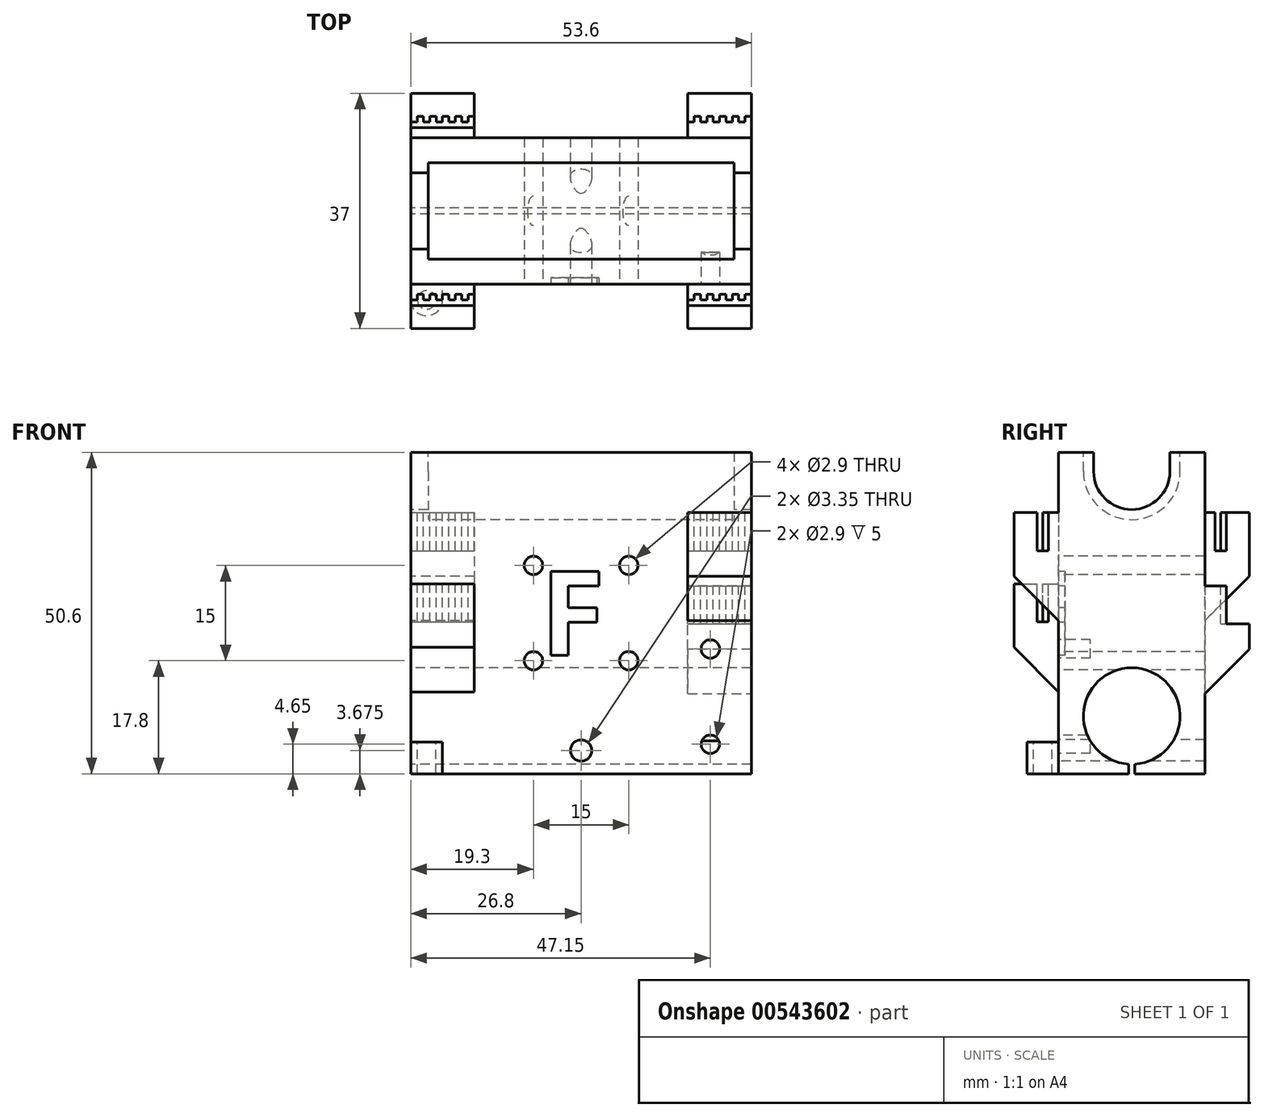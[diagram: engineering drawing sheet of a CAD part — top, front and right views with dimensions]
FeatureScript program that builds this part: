
annotation { "Feature Type Name" : "Feature", "Feature Type Description" : "" }
export const myFeature = defineFeature(function(context is Context, id is Id, definition is map)
    precondition{}
    {
        {
            assignVariable(context, id + "F0", {"name" : "LM8LUU", "anyValue" : 1.8});
        }
        {
            var Q0;
            Q0=qCreatedBy(makeId("Top.planeOp"),FACE);
            var sketch = newSketch(context, id + "F1", { "sketchPlane" : qUnion([Q0])});
            skLineSegment(sketch, "E0.bottom", {"start": v(0, 0) * mm, "end": v(53.6, 0) * mm});
            skLineSegment(sketch, "E0.top", {"start": v(0, 23) * mm, "end": v(53.6, 23) * mm});
            skLineSegment(sketch, "E0.left", {"start": v(0, 0) * mm, "end": v(0, 23) * mm});
            skLineSegment(sketch, "E0.right", {"start": v(53.6, 0) * mm, "end": v(53.6, 23) * mm});
            skSolve(sketch);
        }
        {
            var Q0;
            Q0=qSketchRegion(id+"F1",true);
            extrude(context, id + "F2", {"entities" : qUnion([Q0]), "depth" : 50.6 * mm});
        }
        {
            var Q0;
            Q0=makeQuery(id+"F2.opExtrude","SWEPT_FACE",FACE,{"disambiguationData":[OSD([sQuery(id+"F1.wireOp",EDGE,"E0.left")])]});
            var sketch = newSketch(context, id + "F3", { "sketchPlane" : qUnion([Q0])});
            skCircle(sketch, "E1", {"center": v(-11.5, 9.1) * mm, "radius": 7.6 * mm});
            skCircle(sketch, "E2", {"center": v(-11.5, 47.6) * mm, "radius": 6 * mm});
            skLineSegment(sketch, "E3", {"start": v(-23, 47.6) * mm, "end": v(0, 47.6) * mm, "construction": true});
            skLineSegment(sketch, "E4", {"start": v(-17.5, 50.6) * mm, "end": v(-17.5, 47.6) * mm});
            skLineSegment(sketch, "E5", {"start": v(-5.5, 50.6) * mm, "end": v(-5.5, 47.6) * mm});
            skLineSegment(sketch, "E6", {"start": v(-23, 9.1) * mm, "end": v(0, 9.1) * mm, "construction": true});
            skLineSegment(sketch, "E7", {"start": v(-11.5, 9.1) * mm, "end": v(-11.5, 0) * mm, "construction": true});
            skLineSegment(sketch, "E8", {"start": v(-11.5, 0) * mm, "end": v(-12, 0) * mm});
            skLineSegment(sketch, "E9", {"start": v(-12, 0) * mm, "end": v(-12, 1.52) * mm});
            skLineSegment(sketch, "E10", {"start": v(-12, 1.52) * mm, "end": v(-11, 1.52) * mm});
            skLineSegment(sketch, "E11", {"start": v(-11, 1.52) * mm, "end": v(-11, 0) * mm});
            skLineSegment(sketch, "E12", {"start": v(-11, 0) * mm, "end": v(-11.5, 0) * mm});
            skLineSegment(sketch, "E13", {"start": v(-11.5, 15.6) * mm, "end": v(-11.5, 16.7) * mm});
            skLineSegment(sketch, "E14", {"start": v(-11.5, 15.6) * mm, "end": v(-7, 15.22) * mm});
            skLineSegment(sketch, "E15", {"start": v(-11.5, 15.6) * mm, "end": v(-16, 15.22) * mm});
            skCircle(sketch, "E16", {"center": v(-11.5, 47.6) * mm, "radius": 7.6 * mm});
            skLineSegment(sketch, "E17", {"start": v(-3.9, 47.6) * mm, "end": v(-3.9, 50.6) * mm});
            skLineSegment(sketch, "E18", {"start": v(-19.1, 47.6) * mm, "end": v(-19.1, 50.6) * mm});
            skSolve(sketch);
        }
        {
            var Q0;
            {var subQ0=sQuery(id+"F3.wireOp",EDGE,"E14");var subQ1=sQuery(id+"F3.wireOp",EDGE,"E1");var subQ3=makeQuery(id+"F3.imprint","INTERSECT",VERTEX,{"disambiguationData":[OD(0.0)],"derivedFrom":[subQ1,subQ0]});Q0=makeQuery(id+"F3.imprint","IMPRINT",FACE,{"disambiguationData":[TD([[makeQuery(id+"F3.imprint","IMPRINT",EDGE,{"disambiguationData":[TD([[subQ3,-1.0]])],"derivedFrom":subQ1}),1.0]])]});}
            var Q1;
            {var subQ0=sQuery(id+"F3.wireOp",EDGE,"E15");var subQ1=sQuery(id+"F3.wireOp",EDGE,"E1");var subQ3=makeQuery(id+"F3.imprint","INTERSECT",VERTEX,{"disambiguationData":[OD(0.0)],"derivedFrom":[subQ1,subQ0]});Q1=makeQuery(id+"F3.imprint","IMPRINT",FACE,{"disambiguationData":[TD([[makeQuery(id+"F3.imprint","IMPRINT",EDGE,{"disambiguationData":[TD([[subQ3,1.0]])],"derivedFrom":subQ1}),1.0]])]});}
            var Q2;
            Q2=makeQuery(id+"F3.imprint","IMPRINT",FACE,{"disambiguationData":[TD([[makeQuery(id+"F3.imprint","IMPRINT",EDGE,{"derivedFrom":sQuery(id+"F3.wireOp",EDGE,"E8")}),-1.0]])]});
            var Q3;
            {var subQ0=sQuery(id+"F3.wireOp",EDGE,"E10");Q3=makeQuery(id+"F3.imprint","IMPRINT",FACE,{"disambiguationData":[TD([[makeQuery(id+"F3.imprint","IMPRINT",EDGE,{"derivedFrom":subQ0}),-1.0]])]});}
            var Q4;
            {var subQ3=sQuery(id+"F3.wireOp",EDGE,"E13");Q4=makeQuery(id+"F3.imprint","IMPRINT",FACE,{"disambiguationData":[TD([[makeQuery(id+"F3.imprint","IMPRINT",EDGE,{"derivedFrom":subQ3}),-1.0]])]});}
            var Q5;
            {var subQ3=sQuery(id+"F3.wireOp",EDGE,"E13");Q5=makeQuery(id+"F3.imprint","IMPRINT",FACE,{"disambiguationData":[TD([[makeQuery(id+"F3.imprint","IMPRINT",EDGE,{"derivedFrom":subQ3}),1.0]])]});}
            var Q6;
            {var subQ7=sQuery(id+"F3.wireOp",EDGE,"E10");Q6=makeQuery(id+"F3.imprint","IMPRINT",FACE,{"disambiguationData":[TD([[makeQuery(id+"F3.imprint","IMPRINT",EDGE,{"derivedFrom":subQ7}),1.0]])]});}
            var Q7;
            {var subQ3=sQuery(id+"F3.wireOp",EDGE,"E5");Q7=makeQuery(id+"F3.imprint","IMPRINT",FACE,{"disambiguationData":[TD([[makeQuery(id+"F3.imprint","IMPRINT",EDGE,{"derivedFrom":subQ3}),-1.0]])]});}
            var Q8;
            {var subQ0=sQuery(id+"F3.wireOp",EDGE,"E4");Q8=makeQuery(id+"F3.imprint","IMPRINT",FACE,{"disambiguationData":[TD([[makeQuery(id+"F3.imprint","IMPRINT",EDGE,{"derivedFrom":subQ0}),1.0]])]});}
            var Q9;
            {var subQ0=sQuery(id+"F3.wireOp",EDGE,"E4");Q9=makeQuery(id+"F3.imprint","IMPRINT",FACE,{"disambiguationData":[TD([[makeQuery(id+"F3.imprint","IMPRINT",EDGE,{"derivedFrom":subQ0}),1.0]])]});}
            var Q10;
            {var subQ3=sQuery(id+"F3.wireOp",EDGE,"E5");Q10=makeQuery(id+"F3.imprint","IMPRINT",FACE,{"disambiguationData":[TD([[makeQuery(id+"F3.imprint","IMPRINT",EDGE,{"derivedFrom":subQ3}),-1.0]])]});}
            var Q11;
            {var subQ1=sQuery(id+"F3.wireOp",EDGE,"E2");var subQ4=makeQuery(id+"F3.imprint","INTERSECT",VERTEX,{"derivedFrom":[subQ1,sQuery(id+"F3.wireOp",EDGE,"E5")]});Q11=makeQuery(id+"F3.imprint","IMPRINT",FACE,{"disambiguationData":[TD([[makeQuery(id+"F3.imprint","IMPRINT",EDGE,{"disambiguationData":[TD([[subQ4,-1.0]])],"derivedFrom":subQ1}),1.0]])]});}
            extrude(context, id + "F4", {"entities" : qUnion([Q0, Q1, Q2, Q3, Q4, Q5, Q6, Q7, Q8, Q9, Q10, Q11]), "operationType" : NewBodyOperationType.REMOVE, "endBound" : BoundingType.THROUGH_ALL, "oppositeDirection" : true, "depth" : 25 * mm});
        }
        {
            var Q0;
            {var subQ3=sQuery(id+"F3.wireOp",EDGE,"E4");Q0=makeQuery(id+"F3.imprint","IMPRINT",FACE,{"disambiguationData":[TD([[makeQuery(id+"F3.imprint","IMPRINT",EDGE,{"derivedFrom":subQ3}),-1.0]])]});}
            var Q1;
            {var subQ3=sQuery(id+"F3.wireOp",EDGE,"E18");Q1=makeQuery(id+"F3.imprint","IMPRINT",FACE,{"disambiguationData":[TD([[makeQuery(id+"F3.imprint","IMPRINT",EDGE,{"derivedFrom":subQ3}),-1.0]])]});}
            var Q2;
            {var subQ3=sQuery(id+"F3.wireOp",EDGE,"E17");Q2=makeQuery(id+"F3.imprint","IMPRINT",FACE,{"disambiguationData":[TD([[makeQuery(id+"F3.imprint","IMPRINT",EDGE,{"derivedFrom":subQ3}),1.0]])]});}
            extrude(context, id + "F5", {"entities" : qUnion([Q0, Q1, Q2]), "operationType" : NewBodyOperationType.REMOVE, "oppositeDirection" : true, "depth" : (46.25 + getVariable(context, 'LM8LUU') * 2) * mm});
        }
        {
            var Q0;
            {var subQ3=sQuery(id+"F3.wireOp",EDGE,"E4");Q0=makeQuery(id+"F3.imprint","IMPRINT",FACE,{"disambiguationData":[TD([[makeQuery(id+"F3.imprint","IMPRINT",EDGE,{"derivedFrom":subQ3}),-1.0]])]});}
            var Q1;
            {var subQ3=sQuery(id+"F3.wireOp",EDGE,"E18");Q1=makeQuery(id+"F3.imprint","IMPRINT",FACE,{"disambiguationData":[TD([[makeQuery(id+"F3.imprint","IMPRINT",EDGE,{"derivedFrom":subQ3}),-1.0]])]});}
            var Q2;
            {var subQ3=sQuery(id+"F3.wireOp",EDGE,"E17");Q2=makeQuery(id+"F3.imprint","IMPRINT",FACE,{"disambiguationData":[TD([[makeQuery(id+"F3.imprint","IMPRINT",EDGE,{"derivedFrom":subQ3}),1.0]])]});}
            extrude(context, id + "F6", {"entities" : qUnion([Q0, Q1, Q2]), "operationType" : NewBodyOperationType.ADD, "oppositeDirection" : true, "depth" : (26.75 - getVariable(context, 'LM8LUU')) * mm});
        }
        {
            var Q0;
            {var subQ3=sQuery(id+"F3.wireOp",EDGE,"E4");Q0=makeQuery(id+"F3.imprint","IMPRINT",FACE,{"disambiguationData":[TD([[makeQuery(id+"F3.imprint","IMPRINT",EDGE,{"derivedFrom":subQ3}),-1.0]])]});}
            var Q1;
            {var subQ3=sQuery(id+"F3.wireOp",EDGE,"E18");Q1=makeQuery(id+"F3.imprint","IMPRINT",FACE,{"disambiguationData":[TD([[makeQuery(id+"F3.imprint","IMPRINT",EDGE,{"derivedFrom":subQ3}),-1.0]])]});}
            var Q2;
            {var subQ3=sQuery(id+"F3.wireOp",EDGE,"E17");Q2=makeQuery(id+"F3.imprint","IMPRINT",FACE,{"disambiguationData":[TD([[makeQuery(id+"F3.imprint","IMPRINT",EDGE,{"derivedFrom":subQ3}),1.0]])]});}
            extrude(context, id + "F7", {"entities" : qUnion([Q0, Q1, Q2]), "operationType" : NewBodyOperationType.REMOVE, "oppositeDirection" : true, "depth" : (23.25 + getVariable(context, 'LM8LUU')) * mm});
        }
        {
            var Q0;
            {var subQ3=sQuery(id+"F3.wireOp",EDGE,"E4");Q0=makeQuery(id+"F3.imprint","IMPRINT",FACE,{"disambiguationData":[TD([[makeQuery(id+"F3.imprint","IMPRINT",EDGE,{"derivedFrom":subQ3}),-1.0]])]});}
            var Q1;
            {var subQ3=sQuery(id+"F3.wireOp",EDGE,"E18");Q1=makeQuery(id+"F3.imprint","IMPRINT",FACE,{"disambiguationData":[TD([[makeQuery(id+"F3.imprint","IMPRINT",EDGE,{"derivedFrom":subQ3}),-1.0]])]});}
            var Q2;
            {var subQ3=sQuery(id+"F3.wireOp",EDGE,"E17");Q2=makeQuery(id+"F3.imprint","IMPRINT",FACE,{"disambiguationData":[TD([[makeQuery(id+"F3.imprint","IMPRINT",EDGE,{"derivedFrom":subQ3}),1.0]])]});}
            extrude(context, id + "F8", {"entities" : qUnion([Q0, Q1, Q2]), "operationType" : NewBodyOperationType.ADD, "oppositeDirection" : true, "depth" : 3.75 * mm});
        }
        {
            var Q0;
            Q0=makeQuery(id+"F2.opExtrude","SWEPT_FACE",FACE,{"disambiguationData":[OSD([sQuery(id+"F1.wireOp",EDGE,"E0.bottom")])]});
            var sketch = newSketch(context, id + "F9", { "sketchPlane" : qUnion([Q0])});
            skLineSegment(sketch, "E19.bottom", {"start": v(0, 29.9) * mm, "end": v(10, 29.9) * mm});
            skLineSegment(sketch, "E19.top", {"start": v(0, 9.9) * mm, "end": v(10, 9.9) * mm});
            skLineSegment(sketch, "E19.left", {"start": v(0, 29.9) * mm, "end": v(0, 9.9) * mm});
            skLineSegment(sketch, "E19.right", {"start": v(10, 29.9) * mm, "end": v(10, 9.9) * mm});
            skLineSegment(sketch, "E20.bottom", {"start": v(53.6, 41.1) * mm, "end": v(43.6, 41.1) * mm});
            skLineSegment(sketch, "E20.top", {"start": v(53.6, 21.1) * mm, "end": v(43.6, 21.1) * mm});
            skLineSegment(sketch, "E20.left", {"start": v(53.6, 41.1) * mm, "end": v(53.6, 21.1) * mm});
            skLineSegment(sketch, "E20.right", {"start": v(43.6, 41.1) * mm, "end": v(43.6, 21.1) * mm});
            skPoint(sketch, "E21", {"position": v(0, 47.6) * mm});
            skPoint(sketch, "E22", {"position": v(0, 9.4) * mm});
            skSolve(sketch);
        }
        {
            var Q0;
            Q0=qSketchRegion(id+"F9",true);
            extrude(context, id + "F10", {"entities" : qUnion([Q0]), "operationType" : NewBodyOperationType.ADD, "depth" : 7 * mm});
        }
        {
            var Q0;
            Q0=makeQuery(id+"F10.opExtrude","CAP_EDGE",EDGE,{"disambiguationData":[OSD([sQuery(id+"F9.wireOp",EDGE,"E19.top")])],"isStart":false});
            var Q1;
            Q1=makeQuery(id+"F10.opExtrude","CAP_EDGE",EDGE,{"disambiguationData":[OSD([sQuery(id+"F9.wireOp",EDGE,"E20.top")])],"isStart":false});
            chamfer(context, id + "F11", {"entities" : qUnion([Q0, Q1]), "width" : 10 * mm, "tangentPropagation" : true});
        }
        {
            var Q0;
            Q0=makeQuery(id+"F10.opExtrude","SWEPT_FACE",FACE,{"disambiguationData":[OSD([sQuery(id+"F9.wireOp",EDGE,"E19.bottom")])]});
            var sketch = newSketch(context, id + "F12", { "sketchPlane" : qUnion([Q0])});
            skLineSegment(sketch, "E23", {"start": v(-935.9, 0) * mm, "end": v(-935.88, -4.54) * mm});
            skLineSegment(sketch, "E24.left", {"start": v(0, -3.4) * mm, "end": v(0, -1.6) * mm});
            skLineSegment(sketch, "E25", {"start": v(6, -2.5) * mm, "end": v(7, -2.5) * mm});
            skLineSegment(sketch, "E26", {"start": v(4, -2.5) * mm, "end": v(5, -2.5) * mm});
            skLineSegment(sketch, "E27", {"start": v(0, -2.5) * mm, "end": v(1, -2.5) * mm});
            skLineSegment(sketch, "E28", {"start": v(7, -1.6) * mm, "end": v(8, -1.6) * mm});
            skLineSegment(sketch, "E29", {"start": v(2, -2.5) * mm, "end": v(3, -2.5) * mm});
            skLineSegment(sketch, "E30", {"start": v(3, -1.6) * mm, "end": v(4, -1.6) * mm});
            skLineSegment(sketch, "E31", {"start": v(8, -2.5) * mm, "end": v(9, -2.5) * mm});
            skLineSegment(sketch, "E32", {"start": v(8, -1.6) * mm, "end": v(8, -2.5) * mm});
            skLineSegment(sketch, "E33", {"start": v(9, -2.5) * mm, "end": v(9, -1.6) * mm});
            skLineSegment(sketch, "E34", {"start": v(10, -1.6) * mm, "end": v(10, -2.5) * mm});
            skLineSegment(sketch, "E35", {"start": v(6, -1.6) * mm, "end": v(6, -2.5) * mm});
            skLineSegment(sketch, "E36", {"start": v(2, -1.6) * mm, "end": v(2, -2.5) * mm});
            skLineSegment(sketch, "E37", {"start": v(1, -1.6) * mm, "end": v(2, -1.6) * mm});
            skLineSegment(sketch, "E38", {"start": v(1, -2.5) * mm, "end": v(1, -1.6) * mm});
            skLineSegment(sketch, "E39", {"start": v(9, -1.6) * mm, "end": v(10, -1.6) * mm});
            skLineSegment(sketch, "E40", {"start": v(5, -1.6) * mm, "end": v(6, -1.6) * mm});
            skLineSegment(sketch, "E41", {"start": v(5, -2.5) * mm, "end": v(5, -1.6) * mm});
            skLineSegment(sketch, "E42", {"start": v(3, -2.5) * mm, "end": v(3, -1.6) * mm});
            skLineSegment(sketch, "E43", {"start": v(4, -1.6) * mm, "end": v(4, -2.5) * mm});
            skLineSegment(sketch, "E44", {"start": v(7, -2.5) * mm, "end": v(7, -1.6) * mm});
            skLineSegment(sketch, "E45", {"start": v(0, -1.6) * mm, "end": v(0, -2.5) * mm});
            skLineSegment(sketch, "E46", {"start": v(10, -2.5) * mm, "end": v(10, -3.4) * mm});
            skLineSegment(sketch, "E47", {"start": v(0, -3.4) * mm, "end": v(10, -3.4) * mm});
            skLineSegment(sketch, "E48", {"start": v(5.3, -1.6) * mm, "end": v(5.3, 0) * mm});
            skSolve(sketch);
        }
        {
            var Q0;
            Q0=qSketchRegion(id+"F12",true);
            extrude(context, id + "F13", {"entities" : qUnion([Q0]), "operationType" : NewBodyOperationType.REMOVE, "oppositeDirection" : true, "depth" : 6 * mm});
        }
        {
            var Q0;
            Q0=makeQuery(id+"F10.opExtrude","SWEPT_FACE",FACE,{"disambiguationData":[OSD([sQuery(id+"F9.wireOp",EDGE,"E20.bottom")])]});
            var sketch = newSketch(context, id + "F14", { "sketchPlane" : qUnion([Q0])});
            skLineSegment(sketch, "E49.left", {"start": v(43.6, -3.4) * mm, "end": v(43.6, -1.6) * mm});
            skLineSegment(sketch, "E50", {"start": v(49.6, -2.5) * mm, "end": v(50.6, -2.5) * mm});
            skLineSegment(sketch, "E51", {"start": v(47.6, -2.5) * mm, "end": v(48.6, -2.5) * mm});
            skLineSegment(sketch, "E52", {"start": v(43.6, -2.5) * mm, "end": v(44.6, -2.5) * mm});
            skLineSegment(sketch, "E53", {"start": v(50.6, -1.6) * mm, "end": v(51.6, -1.6) * mm});
            skLineSegment(sketch, "E54", {"start": v(45.6, -2.5) * mm, "end": v(46.6, -2.5) * mm});
            skLineSegment(sketch, "E55", {"start": v(46.6, -1.6) * mm, "end": v(47.6, -1.6) * mm});
            skLineSegment(sketch, "E56", {"start": v(51.6, -2.5) * mm, "end": v(52.6, -2.5) * mm});
            skLineSegment(sketch, "E57", {"start": v(51.6, -1.6) * mm, "end": v(51.6, -2.5) * mm});
            skLineSegment(sketch, "E58", {"start": v(52.6, -2.5) * mm, "end": v(52.6, -1.6) * mm});
            skLineSegment(sketch, "E59", {"start": v(53.6, -1.6) * mm, "end": v(53.6, -2.5) * mm});
            skLineSegment(sketch, "E60", {"start": v(49.6, -1.6) * mm, "end": v(49.6, -2.5) * mm});
            skLineSegment(sketch, "E61", {"start": v(45.6, -1.6) * mm, "end": v(45.6, -2.5) * mm});
            skLineSegment(sketch, "E62", {"start": v(44.6, -1.6) * mm, "end": v(45.6, -1.6) * mm});
            skLineSegment(sketch, "E63", {"start": v(44.6, -2.5) * mm, "end": v(44.6, -1.6) * mm});
            skLineSegment(sketch, "E64", {"start": v(52.6, -1.6) * mm, "end": v(53.6, -1.6) * mm});
            skLineSegment(sketch, "E65", {"start": v(48.6, -1.6) * mm, "end": v(49.6, -1.6) * mm});
            skLineSegment(sketch, "E66", {"start": v(48.6, -2.5) * mm, "end": v(48.6, -1.6) * mm});
            skLineSegment(sketch, "E67", {"start": v(46.6, -2.5) * mm, "end": v(46.6, -1.6) * mm});
            skLineSegment(sketch, "E68", {"start": v(47.6, -1.6) * mm, "end": v(47.6, -2.5) * mm});
            skLineSegment(sketch, "E69", {"start": v(50.6, -2.5) * mm, "end": v(50.6, -1.6) * mm});
            skLineSegment(sketch, "E70", {"start": v(43.6, -1.6) * mm, "end": v(43.6, -2.5) * mm});
            skLineSegment(sketch, "E71", {"start": v(53.6, -2.5) * mm, "end": v(53.6, -3.4) * mm});
            skLineSegment(sketch, "E72", {"start": v(43.6, -3.4) * mm, "end": v(53.6, -3.4) * mm});
            skLineSegment(sketch, "E73", {"start": v(48.83, -1.6) * mm, "end": v(48.83, 0) * mm});
            skSolve(sketch);
        }
        {
            var Q0;
            Q0=qSketchRegion(id+"F14",true);
            extrude(context, id + "F15", {"entities" : qUnion([Q0]), "operationType" : NewBodyOperationType.REMOVE, "oppositeDirection" : true, "depth" : 6 * mm});
        }
        {
            var Q0;
            Q0=makeQuery(id+"F2.opExtrude","SWEPT_FACE",FACE,{"disambiguationData":[OSD([sQuery(id+"F1.wireOp",EDGE,"E0.top")])]});
            var sketch = newSketch(context, id + "F16", { "sketchPlane" : qUnion([Q0])});
            skLineSegment(sketch, "E74.bottom", {"start": v(-53.6, 9.6) * mm, "end": v(-43.6, 9.6) * mm});
            skLineSegment(sketch, "E74.top", {"start": v(-53.6, 29.6) * mm, "end": v(-43.6, 29.6) * mm});
            skLineSegment(sketch, "E74.left", {"start": v(-53.6, 9.6) * mm, "end": v(-53.6, 29.6) * mm});
            skLineSegment(sketch, "E74.right", {"start": v(-43.6, 9.6) * mm, "end": v(-43.6, 29.6) * mm});
            skLineSegment(sketch, "E75.bottom", {"start": v(0, 41.1) * mm, "end": v(-10, 41.1) * mm});
            skLineSegment(sketch, "E75.top", {"start": v(0, 21.1) * mm, "end": v(-10, 21.1) * mm});
            skLineSegment(sketch, "E75.left", {"start": v(0, 41.1) * mm, "end": v(0, 21.1) * mm});
            skLineSegment(sketch, "E75.right", {"start": v(-10, 41.1) * mm, "end": v(-10, 21.1) * mm});
            skSolve(sketch);
        }
        {
            var Q0;
            Q0=qSketchRegion(id+"F16",true);
            extrude(context, id + "F17", {"entities" : qUnion([Q0]), "operationType" : NewBodyOperationType.ADD, "depth" : 7 * mm});
        }
        {
            var Q0;
            Q0=makeQuery(id+"F17.opExtrude","SWEPT_FACE",FACE,{"disambiguationData":[OSD([sQuery(id+"F16.wireOp",EDGE,"E74.top")])]});
            var sketch = newSketch(context, id + "F18", { "sketchPlane" : qUnion([Q0])});
            skLineSegment(sketch, "E76.left", {"start": v(43.6, 24.6) * mm, "end": v(43.6, 26.4) * mm});
            skLineSegment(sketch, "E77", {"start": v(49.6, 25.5) * mm, "end": v(50.6, 25.5) * mm});
            skLineSegment(sketch, "E78", {"start": v(47.6, 25.5) * mm, "end": v(48.6, 25.5) * mm});
            skLineSegment(sketch, "E79", {"start": v(43.6, 25.5) * mm, "end": v(44.6, 25.5) * mm});
            skLineSegment(sketch, "E80", {"start": v(50.6, 26.4) * mm, "end": v(51.6, 26.4) * mm});
            skLineSegment(sketch, "E81", {"start": v(45.6, 25.5) * mm, "end": v(46.6, 25.5) * mm});
            skLineSegment(sketch, "E82", {"start": v(46.6, 26.4) * mm, "end": v(47.6, 26.4) * mm});
            skLineSegment(sketch, "E83", {"start": v(51.6, 25.5) * mm, "end": v(52.6, 25.5) * mm});
            skLineSegment(sketch, "E84", {"start": v(51.6, 26.4) * mm, "end": v(51.6, 25.5) * mm});
            skLineSegment(sketch, "E85", {"start": v(52.6, 25.5) * mm, "end": v(52.6, 26.4) * mm});
            skLineSegment(sketch, "E86", {"start": v(53.6, 26.4) * mm, "end": v(53.6, 25.5) * mm});
            skLineSegment(sketch, "E87", {"start": v(49.6, 26.4) * mm, "end": v(49.6, 25.5) * mm});
            skLineSegment(sketch, "E88", {"start": v(45.6, 26.4) * mm, "end": v(45.6, 25.5) * mm});
            skLineSegment(sketch, "E89", {"start": v(44.6, 26.4) * mm, "end": v(45.6, 26.4) * mm});
            skLineSegment(sketch, "E90", {"start": v(44.6, 25.5) * mm, "end": v(44.6, 26.4) * mm});
            skLineSegment(sketch, "E91", {"start": v(52.6, 26.4) * mm, "end": v(53.6, 26.4) * mm});
            skLineSegment(sketch, "E92", {"start": v(48.6, 26.4) * mm, "end": v(49.6, 26.4) * mm});
            skLineSegment(sketch, "E93", {"start": v(48.6, 25.5) * mm, "end": v(48.6, 26.4) * mm});
            skLineSegment(sketch, "E94", {"start": v(46.6, 25.5) * mm, "end": v(46.6, 26.4) * mm});
            skLineSegment(sketch, "E95", {"start": v(47.6, 26.4) * mm, "end": v(47.6, 25.5) * mm});
            skLineSegment(sketch, "E96", {"start": v(50.6, 25.5) * mm, "end": v(50.6, 26.4) * mm});
            skLineSegment(sketch, "E97", {"start": v(43.6, 26.4) * mm, "end": v(43.6, 25.5) * mm});
            skLineSegment(sketch, "E98", {"start": v(53.6, 25.5) * mm, "end": v(53.6, 24.6) * mm});
            skLineSegment(sketch, "E99", {"start": v(43.6, 24.6) * mm, "end": v(53.6, 24.6) * mm});
            skLineSegment(sketch, "E100", {"start": v(48.6, 24.6) * mm, "end": v(48.6, 23) * mm});
            skSolve(sketch);
        }
        {
            var Q0;
            {var subQ4=sQuery(id+"F18.wireOp",EDGE,"E76.left");Q0=makeQuery(id+"F18.imprint","IMPRINT",FACE,{"disambiguationData":[TD([[makeQuery(id+"F18.imprint","IMPRINT",EDGE,{"derivedFrom":subQ4}),1.0]])]});}
            extrude(context, id + "F19", {"entities" : qUnion([Q0]), "operationType" : NewBodyOperationType.REMOVE, "oppositeDirection" : true, "depth" : 6 * mm});
        }
        {
            var Q0;
            Q0=makeQuery(id+"F17.opExtrude","SWEPT_FACE",FACE,{"disambiguationData":[OSD([sQuery(id+"F16.wireOp",EDGE,"E75.bottom")])]});
            var sketch = newSketch(context, id + "F20", { "sketchPlane" : qUnion([Q0])});
            skLineSegment(sketch, "E101", {"start": v(6, 25.5) * mm, "end": v(7, 25.5) * mm});
            skLineSegment(sketch, "E102", {"start": v(4, 25.5) * mm, "end": v(5, 25.5) * mm});
            skLineSegment(sketch, "E103", {"start": v(0, 25.5) * mm, "end": v(1, 25.5) * mm});
            skLineSegment(sketch, "E104", {"start": v(7, 26.4) * mm, "end": v(8, 26.4) * mm});
            skLineSegment(sketch, "E105", {"start": v(2, 25.5) * mm, "end": v(3, 25.5) * mm});
            skLineSegment(sketch, "E106", {"start": v(3, 26.4) * mm, "end": v(4, 26.4) * mm});
            skLineSegment(sketch, "E107", {"start": v(8, 25.5) * mm, "end": v(9, 25.5) * mm});
            skLineSegment(sketch, "E108", {"start": v(8, 26.4) * mm, "end": v(8, 25.5) * mm});
            skLineSegment(sketch, "E109", {"start": v(9, 25.5) * mm, "end": v(9, 26.4) * mm});
            skLineSegment(sketch, "E110", {"start": v(10, 26.4) * mm, "end": v(10, 25.5) * mm});
            skLineSegment(sketch, "E111", {"start": v(6, 26.4) * mm, "end": v(6, 25.5) * mm});
            skLineSegment(sketch, "E112", {"start": v(2, 26.4) * mm, "end": v(2, 25.5) * mm});
            skLineSegment(sketch, "E113", {"start": v(1, 26.4) * mm, "end": v(2, 26.4) * mm});
            skLineSegment(sketch, "E114", {"start": v(1, 25.5) * mm, "end": v(1, 26.4) * mm});
            skLineSegment(sketch, "E115", {"start": v(9, 26.4) * mm, "end": v(10, 26.4) * mm});
            skLineSegment(sketch, "E116", {"start": v(5, 26.4) * mm, "end": v(6, 26.4) * mm});
            skLineSegment(sketch, "E117", {"start": v(5, 25.5) * mm, "end": v(5, 26.4) * mm});
            skLineSegment(sketch, "E118", {"start": v(3, 25.5) * mm, "end": v(3, 26.4) * mm});
            skLineSegment(sketch, "E119", {"start": v(4, 26.4) * mm, "end": v(4, 25.5) * mm});
            skLineSegment(sketch, "E120", {"start": v(7, 25.5) * mm, "end": v(7, 26.4) * mm});
            skLineSegment(sketch, "E121", {"start": v(10, 25.5) * mm, "end": v(10, 24.6) * mm});
            skLineSegment(sketch, "E122", {"start": v(0, 24.6) * mm, "end": v(10, 24.6) * mm});
            skLineSegment(sketch, "E123", {"start": v(5, 24.6) * mm, "end": v(5, 23) * mm});
            skLineSegment(sketch, "E124", {"start": v(0, 24.6) * mm, "end": v(0, 25.5) * mm});
            skSolve(sketch);
        }
        {
            var Q0;
            Q0=makeQuery(id+"F20.imprint","IMPRINT",FACE,{"disambiguationData":[TD([[makeQuery(id+"F20.imprint","IMPRINT",EDGE,{"derivedFrom":sQuery(id+"F20.wireOp",EDGE,"E101")}),-1.0]])]});
            extrude(context, id + "F21", {"entities" : qUnion([Q0]), "operationType" : NewBodyOperationType.REMOVE, "oppositeDirection" : true, "depth" : 6 * mm});
        }
        {
            var Q0;
            Q0=makeQuery(id+"F17.opExtrude","CAP_EDGE",EDGE,{"disambiguationData":[OSD([sQuery(id+"F16.wireOp",EDGE,"E75.top")])],"isStart":false});
            var Q1;
            Q1=makeQuery(id+"F17.opExtrude","CAP_EDGE",EDGE,{"disambiguationData":[OSD([sQuery(id+"F16.wireOp",EDGE,"E74.bottom")])],"isStart":false});
            chamfer(context, id + "F22", {"entities" : qUnion([Q0, Q1]), "width" : 10 * mm, "tangentPropagation" : true});
        }
        {
            var Q0;
            Q0=makeQuery(id+"F2.opExtrude","SWEPT_FACE",FACE,{"disambiguationData":[OSD([sQuery(id+"F1.wireOp",EDGE,"E0.bottom")])]});
            var sketch = newSketch(context, id + "F23", { "sketchPlane" : qUnion([Q0])});
            skCircle(sketch, "E125", {"center": v(19.3, 32.8) * mm, "radius": 1.45 * mm});
            skCircle(sketch, "E126", {"center": v(34.3, 32.8) * mm, "radius": 1.45 * mm});
            skCircle(sketch, "E127", {"center": v(19.3, 17.8) * mm, "radius": 1.45 * mm});
            skCircle(sketch, "E128", {"center": v(34.3, 17.8) * mm, "radius": 1.45 * mm});
            skLineSegment(sketch, "E129", {"start": v(19.3, 32.8) * mm, "end": v(0, 32.8) * mm});
            skLineSegment(sketch, "E130", {"start": v(34.3, 17.8) * mm, "end": v(53.6, 17.8) * mm});
            skLineSegment(sketch, "E131", {"start": v(34.3, 32.8) * mm, "end": v(34.3, 50.6) * mm});
            skLineSegment(sketch, "E132", {"start": v(19.3, 17.8) * mm, "end": v(19.3, 0) * mm});
            skCircle(sketch, "E133", {"center": v(26.8, 3.68) * mm, "radius": 1.68 * mm});
            skLineSegment(sketch, "E134", {"start": v(26.8, 0) * mm, "end": v(26.8, 13.82) * mm, "construction": true});
            skSolve(sketch);
        }
        {
            var Q0;
            Q0=qSketchRegion(id+"F23",true);
            var Q1;
            Q1=makeQuery(id+"F23.imprint","IMPRINT",FACE,{"disambiguationData":[TD([[makeQuery(id+"F23.imprint","IMPRINT",EDGE,{"derivedFrom":sQuery(id+"F23.wireOp",EDGE,"E125")}),1.0]])]});
            var Q2;
            Q2=makeQuery(id+"F23.imprint","IMPRINT",FACE,{"disambiguationData":[TD([[makeQuery(id+"F23.imprint","IMPRINT",EDGE,{"derivedFrom":sQuery(id+"F23.wireOp",EDGE,"E126")}),1.0]])]});
            var Q3;
            Q3=makeQuery(id+"F23.imprint","IMPRINT",FACE,{"disambiguationData":[TD([[makeQuery(id+"F23.imprint","IMPRINT",EDGE,{"derivedFrom":sQuery(id+"F23.wireOp",EDGE,"E128")}),1.0]])]});
            var Q4;
            Q4=makeQuery(id+"F23.imprint","IMPRINT",FACE,{"disambiguationData":[TD([[makeQuery(id+"F23.imprint","IMPRINT",EDGE,{"derivedFrom":sQuery(id+"F23.wireOp",EDGE,"E127")}),1.0]])]});
            extrude(context, id + "F24", {"entities" : qUnion([Q0, Q1, Q2, Q3, Q4]), "operationType" : NewBodyOperationType.REMOVE, "endBound" : BoundingType.THROUGH_ALL, "oppositeDirection" : true, "depth" : 25 * mm});
        }
        {
            var Q0;
            Q0=makeQuery(id+"F2.opExtrude","SWEPT_FACE",FACE,{"disambiguationData":[OSD([sQuery(id+"F1.wireOp",EDGE,"E0.bottom")])]});
            var sketch = newSketch(context, id + "F25", { "sketchPlane" : qUnion([Q0])});
            skCircle(sketch, "E135", {"center": v(47.15, 19.65) * mm, "radius": 1.45 * mm});
            skCircle(sketch, "E136", {"center": v(47.15, 4.65) * mm, "radius": 1.45 * mm});
            skSolve(sketch);
        }
        {
            var Q0;
            Q0=qSketchRegion(id+"F25",true);
            extrude(context, id + "F26", {"entities" : qUnion([Q0]), "operationType" : NewBodyOperationType.REMOVE, "oppositeDirection" : true, "depth" : 5 * mm});
        }
        {
            var Q0;
            Q0=makeQuery(id+"F2.opExtrude","SWEPT_FACE",FACE,{"disambiguationData":[OSD([sQuery(id+"F1.wireOp",EDGE,"E0.bottom")])]});
            var sketch = newSketch(context, id + "F27", { "sketchPlane" : qUnion([Q0])});
            skText(sketch, "E137", { "text": "F", "fontName": "OpenSans-Bold.ttf"});
            skLineSegment(sketch, "E138", {"start": v(19.3, 32.8) * mm, "end": v(19.3, 17.8) * mm, "construction": true});
            skLineSegment(sketch, "E139", {"start": v(19.3, 17.8) * mm, "end": v(34.3, 17.8) * mm, "construction": true});
            skLineSegment(sketch, "E140", {"start": v(34.3, 17.8) * mm, "end": v(34.3, 32.8) * mm, "construction": true});
            skLineSegment(sketch, "E141", {"start": v(34.3, 32.8) * mm, "end": v(19.3, 32.8) * mm, "construction": true});
            skLineSegment(sketch, "E142", {"start": v(19.3, 25.3) * mm, "end": v(22.2, 25.3) * mm, "construction": true});
            skLineSegment(sketch, "E143", {"start": v(31.4, 25.3) * mm, "end": v(34.3, 25.3) * mm, "construction": true});
            skLineSegment(sketch, "E144", {"start": v(26.8, 18.66) * mm, "end": v(26.8, 17.8) * mm, "construction": true});
            skLineSegment(sketch, "E145", {"start": v(26.8, 32.8) * mm, "end": v(26.8, 31.94) * mm, "construction": true});
            const initialGuessF27  = {"E137": [0.0204, 0.01866, 1, 0, 0.01328]};
            skSetInitialGuess(sketch, initialGuessF27);
            skSolve(sketch);
        }
        {
            var Q0;
            Q0=qSketchRegion(id+"F27",true);
            extrude(context, id + "F28", {"entities" : qUnion([Q0]), "operationType" : NewBodyOperationType.REMOVE, "oppositeDirection" : true, "depth" : 1 * mm});
        }
        {
            var Q0;
            Q0=makeQuery(id+"F2.opExtrude","SWEPT_FACE",FACE,{"disambiguationData":[OSD([sQuery(id+"F1.wireOp",EDGE,"E0.bottom")])]});
            var sketch = newSketch(context, id + "F29", { "sketchPlane" : qUnion([Q0])});
            skLineSegment(sketch, "E146.bottom", {"start": v(0, 0) * mm, "end": v(5, 0) * mm});
            skLineSegment(sketch, "E146.top", {"start": v(0, 5) * mm, "end": v(5, 5) * mm});
            skLineSegment(sketch, "E146.left", {"start": v(0, 0) * mm, "end": v(0, 5) * mm});
            skLineSegment(sketch, "E146.right", {"start": v(5, 0) * mm, "end": v(5, 5) * mm});
            skSolve(sketch);
        }
        {
            var Q0;
            Q0=qSketchRegion(id+"F29",true);
            extrude(context, id + "F30", {"entities" : qUnion([Q0]), "operationType" : NewBodyOperationType.ADD, "depth" : 5 * mm});
        }
        {
            var Q0;
            Q0=makeQuery(id+"F30.opExtrude","SWEPT_FACE",FACE,{"disambiguationData":[OSD([sQuery(id+"F29.wireOp",EDGE,"E146.top")])]});
            var sketch = newSketch(context, id + "F31", { "sketchPlane" : qUnion([Q0])});
            skCircle(sketch, "E147", {"center": v(2.5, -2.5) * mm, "radius": 1.45 * mm});
            skLineSegment(sketch, "E148", {"start": v(0, -2.5) * mm, "end": v(5, -2.5) * mm});
            skSolve(sketch);
        }
        {
            var Q0;
            Q0=qSketchRegion(id+"F31",true);
            extrude(context, id + "F32", {"entities" : qUnion([Q0]), "operationType" : NewBodyOperationType.REMOVE, "oppositeDirection" : true, "depth" : 25 * mm});
        }
        {
            var Q0;
            Q0=makeQuery(id+"F30.opExtrude","CAP_EDGE",EDGE,{"disambiguationData":[OSD([sQuery(id+"F29.wireOp",EDGE,"E146.left")])],"isStart":false});
            var Q1;
            Q1=makeQuery(id+"F30.opExtrude","CAP_EDGE",EDGE,{"disambiguationData":[OSD([sQuery(id+"F29.wireOp",EDGE,"E146.right")])],"isStart":false});
            fillet(context, id + "F33", {"entities" : qUnion([Q0, Q1]), "radius" : 2.5 * mm, "tangentPropagation" : true, "allowEdgeOverflow" : false});
        }
        {
            var Q0;
            Q0=makeQuery(id+"F5.boolean.opBoolean","COPY",FACE,{"derivedFrom":makeQuery(id+"F5.opExtrude","CAP_FACE",FACE,{"disambiguationData":[OSD([sQuery(id+"F1.wireOp",EDGE,"E0.left"),sQuery(id+"F3.wireOp",EDGE,"E2"),sQuery(id+"F3.wireOp",EDGE,"E4"),sQuery(id+"F3.wireOp",EDGE,"E5"),sQuery(id+"F3.wireOp",EDGE,"E16"),sQuery(id+"F3.wireOp",EDGE,"E17"),sQuery(id+"F3.wireOp",EDGE,"E18")])],"isStart":false})});
            extrude(context, id + "F34", {"entities" : qUnion([Q0]), "operationType" : NewBodyOperationType.REMOVE, "oppositeDirection" : true, "depth" : 1 * mm, "offsetDistance" : 25 * mm});
        }
        {
            var Q0;
            Q0=makeQuery(id+"F8.opExtrude","CAP_FACE",FACE,{"disambiguationData":[OSD([sQuery(id+"F1.wireOp",EDGE,"E0.left"),sQuery(id+"F3.wireOp",EDGE,"E2"),sQuery(id+"F3.wireOp",EDGE,"E4"),sQuery(id+"F3.wireOp",EDGE,"E5"),sQuery(id+"F3.wireOp",EDGE,"E16"),sQuery(id+"F3.wireOp",EDGE,"E17"),sQuery(id+"F3.wireOp",EDGE,"E18")])],"isStart":false});
            extrude(context, id + "F35", {"entities" : qUnion([Q0]), "operationType" : NewBodyOperationType.REMOVE, "oppositeDirection" : true, "depth" : 1 * mm, "offsetDistance" : 25 * mm});
        }
    });
